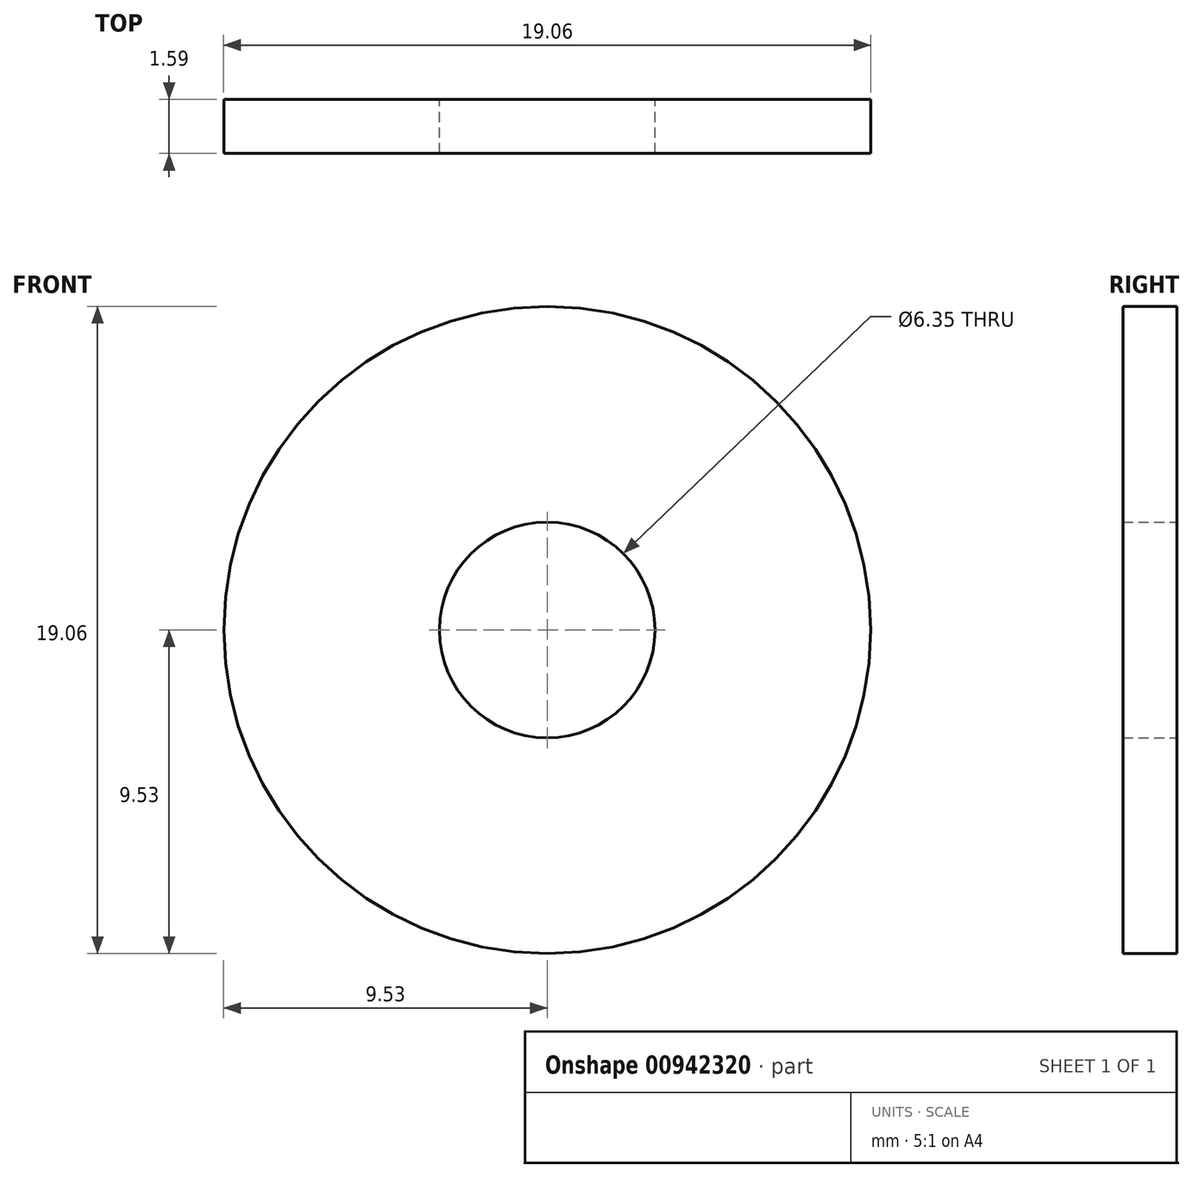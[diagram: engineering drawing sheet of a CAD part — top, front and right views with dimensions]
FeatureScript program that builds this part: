
annotation { "Feature Type Name" : "Feature", "Feature Type Description" : "" }
export const myFeature = defineFeature(function(context is Context, id is Id, definition is map)
    precondition{}
    {
        {
            var Q0;
            Q0=qCreatedBy(makeId("Front.planeOp"),FACE);
            var sketch = newSketch(context, id + "F0", { "sketchPlane" : qUnion([Q0])});
            skCircle(sketch, "E0", {"center": v(0, 0) * mm, "radius": 9.53 * mm});
            skCircle(sketch, "E1", {"center": v(0, 0) * mm, "radius": 3.18 * mm});
            skSolve(sketch);
        }
        {
            var Q0;
            Q0=makeQuery(id+"F0.imprint","IMPRINT",FACE,{"disambiguationData":[TD([[makeQuery(id+"F0.imprint","IMPRINT",EDGE,{"derivedFrom":sQuery(id+"F0.wireOp",EDGE,"E0")}),1.0]])]});
            extrude(context, id + "F1", {"entities" : qUnion([Q0]), "depth" : 1.59 * mm, "offsetDistance" : 25.4 * mm});
        }
    });
